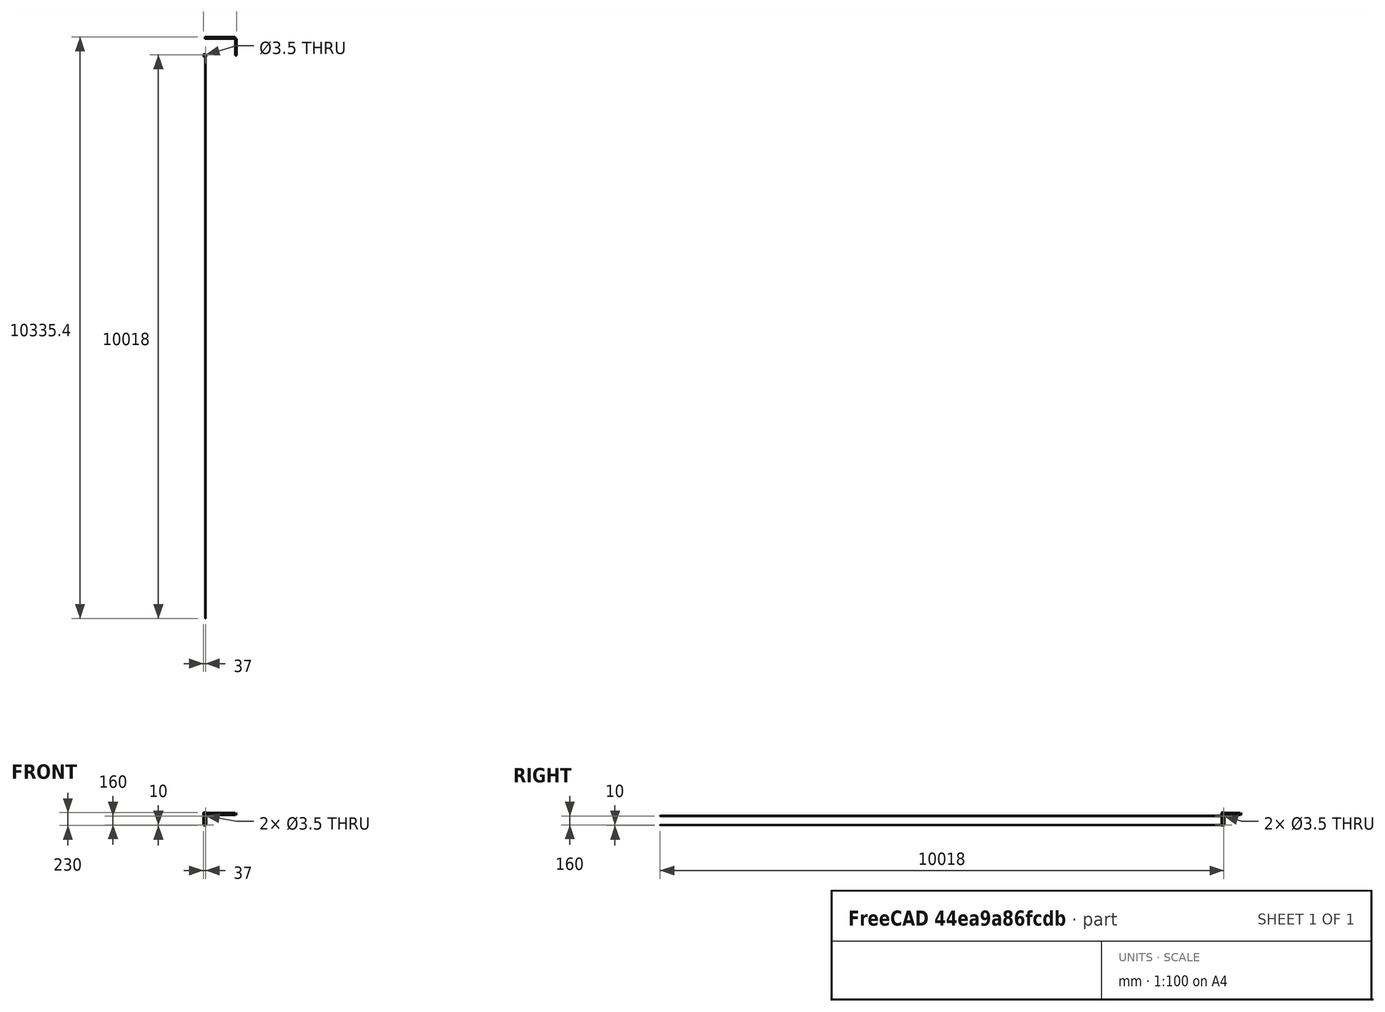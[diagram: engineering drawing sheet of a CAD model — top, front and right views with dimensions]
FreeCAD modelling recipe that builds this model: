
FCSTD DOCUMENT  (FreeCAD 0.14R3702 (Git))
Label: esquina
License: CC-BY 3.0
LicenseURL: http://creativecommons.org/licenses/by/3.0/
objects: Part::Box×9, Sketcher::SketchObject×4, PartDesign::Pocket×3, Part::MultiFuse×2, Part::Cut×2, Part::Cylinder×1, Part::Cone×1, PartDesign::Pad×1, PartDesign::Fillet×1, Mesh::Feature×1
note: 28 computed .brp shape members not serialized (recipe doc carries the construction recipe); baked Part::Feature solids carry a one-line shape summary decoded from their .brp

FEATURE [Part::Cylinder] Cylinder
  Angle = 360
  Height = 230
  Placement = pos=(0,0,-180) rot=(0,0,1;0rad)
  Radius = 27
FEATURE [Part::Box] Box  label="Lateral_Corto_1"
  Height = 40
  Length = 8.5
  Placement = pos=(-7.36122,0,5.25) rot=(0,-1,0;0.523599rad)
  Width = 300
FEATURE [Part::Box] Box001  label="Base"
  Height = 8.5
  Length = 540
  Width = 300
FEATURE [Part::Box] Box002  label="Lateral_Corto_2"
  Height = 40
  Length = 8.5
  Placement = pos=(540,0,8.5) rot=(0,1,0;0.523599rad)
  Width = 300
FEATURE [Part::Box] Box003  label="Lateral_Largo_1"
  Height = 40
  Length = 540
  Placement = pos=(0,300,8.5) rot=(-1,0,0;0.523599rad)
  Width = 8.5
FEATURE [Part::Box] Box004  label="Lateral_Largo_2"
  Height = 40
  Length = 540
  Placement = pos=(0,-7.36122,5.25) rot=(1,0,0;0.523599rad)
  Width = 8.5
FEATURE [Part::Box] Box005  label="Pared_larga"
  Height = 180
  Length = 540
  Placement = pos=(0,-8,-180) rot=(0,0,1;0rad)
  Width = 8.5
FEATURE [Part::Box] Box006  label="Pared_corta"
  Height = 180
  Length = 8.5
  Placement = pos=(-8.5,0,-180) rot=(0,0,1;0rad)
  Width = 300
FEATURE [Part::MultiFuse] Fusion
  Shapes = -> [Box,Box001,Box004,Box006,Box005]
FEATURE [Part::Cone] Cone
  Angle = 360
  Height = 28
  Placement = pos=(10,10,22) rot=(0,0,1;0rad)
  Radius1 = 10
  Radius2 = 24
FEATURE [Part::Box] Box007  label="Cube"
  Height = 230
  Length = 20
  Placement = pos=(-17.9289,-46.2132,-180) rot=(0,0,1;0.785398rad)
  Width = 40
FEATURE [Part::Box] Box008  label="Cube001"
  Height = 180
  Length = 27
  Placement = pos=(0,0,-180) rot=(0,0,1;0rad)
  Width = 27
FEATURE [Sketcher::SketchObject] Sketch
  Placement = pos=(0,0,55) rot=(0,0,1;0rad)
  sketch-geometry (4):
    g0: ArcOfCircle CenterX=10 CenterY=10 CenterZ=0 NormalX=0 NormalY=0 NormalZ=1 Radius=10 StartAngle=2.89503 EndAngle=4.98943
    g1: LineSegment StartX=0.30242 StartY=12.4407 StartZ=0 EndX=6.85799 EndY=38.488 EndZ=0
    g2: LineSegment StartX=38.5705 StartY=7.72766 StartZ=0 EndX=12.7351 EndY=0.381298 EndZ=0
    g3: LineSegment StartX=6.85799 StartY=38.488 StartZ=0 EndX=38.5705 EndY=7.72766 EndZ=0
  constraints (10):
    c: DistanceX(g-1,g0) = 10
    c: DistanceY(g-1,g0) = 10
    c: Tangent(g0,g1)
    c: Coincident(g2,g0)
    c: Tangent(g2,g0)
    c: Radius(g0) = 10
    c: Coincident(g3,g1)
    c: Coincident(g3,g2)
    c: Angle(g1,g3) = 1.0472
    c: Angle(g3,g2) = 1.0472
FEATURE [PartDesign::Pad] Pad
  Length = 43
  Length2 = 100
  Placement = pos=(0,0,55) rot=(0,0,1;0rad)
  Reversed = true
  Sketch = -> Sketch
  Type = 0
FEATURE [Part::MultiFuse] Fusion001
  Shapes = -> [Pad,Fusion,Box007,Box008]
FEATURE [Part::Cut] Cut
  Base = -> Cylinder
  Tool = -> Fusion001
FEATURE [Part::Cut] Cut001
  Base = -> Cut
  Tool = -> Cone
FEATURE [Sketcher::SketchObject] Sketch003
  Placement = pos=(0,0,8.5) rot=(1,0,0;3.14159rad)
  Support = -> Cut001 [Face6]
  sketch-geometry (1):
    g0: Circle CenterX=10 CenterY=-10 CenterZ=0 NormalX=0 NormalY=0 NormalZ=1 Radius=1.75
FEATURE [PartDesign::Pocket] Pocket
  Length = 5
  Sketch = -> Sketch003
  Type = 0
FEATURE [Sketcher::SketchObject] Sketch004
  Placement = pos=(0,-8,0) rot=(0,0.707107,0.707107;3.14159rad)
  Support = -> Pocket [Face21]
  sketch-geometry (2):
    g0: Circle CenterX=-10 CenterY=-10 CenterZ=0 NormalX=0 NormalY=0 NormalZ=1 Radius=1.75
    g1: Circle CenterX=-10 CenterY=-170 CenterZ=0 NormalX=0 NormalY=0 NormalZ=1 Radius=1.75
  constraints (6):
    c: Equal(g1,g0)
    c: Radius(g0) = 1.75
    c: DistanceY(g0,g1) = -160
    c: DistanceX(g-1,g1) = -10
    c: DistanceX(g0) = -10
    c: DistanceY(g-1,g0) = -10
FEATURE [PartDesign::Pocket] Pocket001
  Length = 5
  Sketch = -> Sketch004
  Type = 1
FEATURE [Sketcher::SketchObject] Sketch005
  Placement = pos=(-8.5,0,0) rot=(0.57735,0.57735,0.57735;2.0944rad)
  Support = -> Pocket001 [Face3]
  sketch-geometry (2):
    g0: Circle CenterX=10 CenterY=-10 CenterZ=0 NormalX=0 NormalY=0 NormalZ=1 Radius=1.75
    g1: Circle CenterX=10 CenterY=-170 CenterZ=0 NormalX=0 NormalY=0 NormalZ=1 Radius=1.75
  constraints (6):
    c: Equal(g1,g0)
    c: Radius(g0) = 1.75
    c: DistanceX(g-1,g1) = 10
    c: DistanceY(g0,g1) = -160
    c: DistanceX(g-1,g0) = 10
    c: DistanceY(g-1,g0) = -10
FEATURE [PartDesign::Pocket] Pocket002
  Length = 5
  Sketch = -> Sketch005
  Type = 1
FEATURE [PartDesign::Fillet] Fillet
  Base = -> Pocket002 [Edge11,Edge60,Edge59,Edge47,Edge36,Edge5,Edge31,Edge37]
  Radius = 1
FEATURE [Mesh::Feature] ESQUINA
